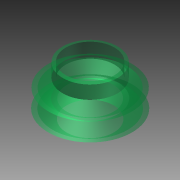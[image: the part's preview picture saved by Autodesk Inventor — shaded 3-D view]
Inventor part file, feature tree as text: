
AUTODESK INVENTOR PART (.ipt)
format: ipt  version: 2011 (Build 150239000, 239)  size: 129,536 bytes
history: native  units: in
note: dims shown in document units (in); Inventor stores cm internally (conversion verified against a paired STEP export)
features: revolve x1, sketch x1
ambient origin geometry x8: Origin, YZ Plane, XZ Plane, XY Plane, X Axis, Y Axis, Z Axis, Center Point
bodies: Solid1 (feature_tree)
feature tree (2):
  revolve  "Revolution1"  Angle=90.0deg
  sketch  "Sketch1"  dims[d0=0.25in d1=0.25in d2=0.2in d3=0.05in d4=0.625in d6=0.25in d9=90.0deg d10=0.0661in d11=0.75in]
